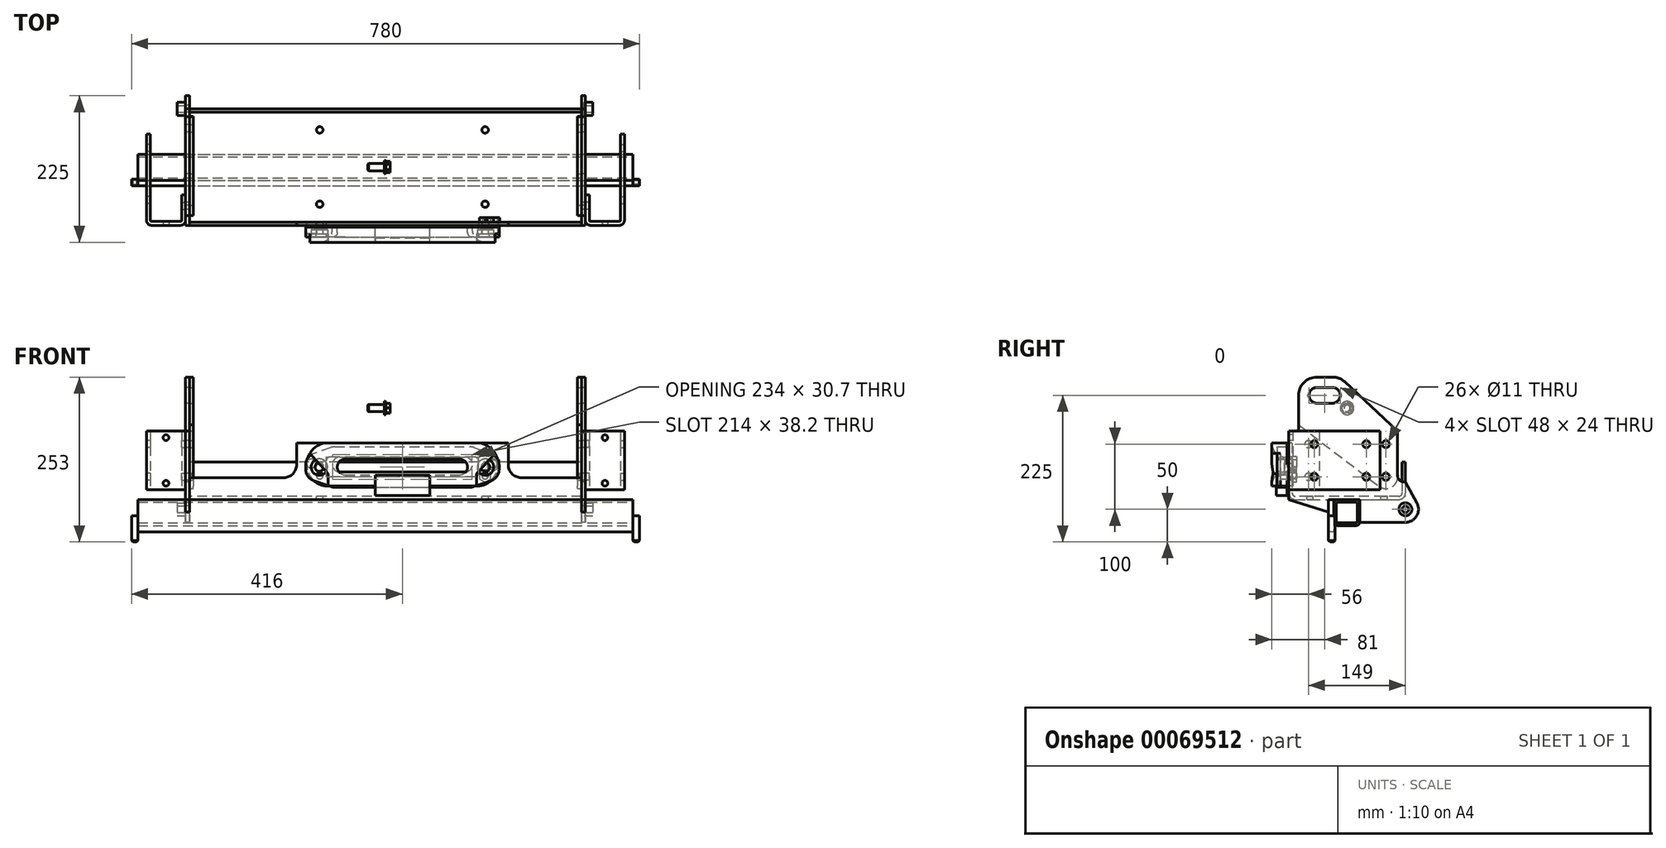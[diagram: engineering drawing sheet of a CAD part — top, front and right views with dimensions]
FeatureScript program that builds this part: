
annotation { "Feature Type Name" : "Feature", "Feature Type Description" : "" }
export const myFeature = defineFeature(function(context is Context, id is Id, definition is map)
    precondition{}
    {
        {
            var Q0;
            Q0=qCreatedBy(makeId("Right.planeOp"),FACE);
            var sketch = newSketch(context, id + "F0", { "sketchPlane" : qUnion([Q0])});
            skLineSegment(sketch, "E0", {"start": v(-84.5, 0) * mm, "end": v(84.5, 0) * mm});
            skLineSegment(sketch, "E1", {"start": v(-84.5, 0) * mm, "end": v(-84.5, 81.8) * mm});
            skLineSegment(sketch, "E2", {"start": v(84.5, 0) * mm, "end": v(84.5, 52.5) * mm});
            skLineSegment(sketch, "E3.0", {"start": v(-89.5, -5) * mm, "end": v(-89.5, 81.8) * mm});
            skLineSegment(sketch, "E3.1", {"start": v(-89.5, -5) * mm, "end": v(89.5, -5) * mm});
            skLineSegment(sketch, "E3.2", {"start": v(89.5, -5) * mm, "end": v(89.5, 52.5) * mm});
            skLineSegment(sketch, "E4", {"start": v(-89.5, 81.8) * mm, "end": v(-84.5, 81.8) * mm});
            skLineSegment(sketch, "E5", {"start": v(84.5, 52.5) * mm, "end": v(89.5, 52.5) * mm});
            skSolve(sketch);
        }
        {
            var Q0;
            Q0 = qSketchRegion(id + "F0", true);
            extrude(context, id + "F1", {"entities" : qUnion([Q0]), "endBound" : BoundingType.SYMMETRIC, "depth" : 896 * mm});
        }
        {
            var Q0;
            Q0=makeQuery(id+"F1.opExtrude","SWEPT_FACE",FACE,{"disambiguationData":[OSD([sQuery(id+"F0.wireOp",EDGE,"E3.0")])]});
            var sketch = newSketch(context, id + "F2", { "sketchPlane" : qUnion([Q0])});
            skLineSegment(sketch, "E6", {"start": v(-448, 28.5) * mm, "end": v(-162.5, 28.5) * mm});
            skLineSegment(sketch, "E7", {"start": v(-162.5, 28.5) * mm, "end": v(-162.5, 81.8) * mm});
            skLineSegment(sketch, "E8", {"start": v(-162.5, 81.8) * mm, "end": v(162.5, 81.8) * mm});
            skLineSegment(sketch, "E9", {"start": v(162.5, 81.8) * mm, "end": v(162.5, 28.5) * mm});
            skLineSegment(sketch, "E10", {"start": v(162.5, 28.5) * mm, "end": v(448, 28.5) * mm});
            skLineSegment(sketch, "E11.bottom", {"start": v(-117, 60.2) * mm, "end": v(117, 60.2) * mm});
            skLineSegment(sketch, "E11.top", {"start": v(-117, 29.5) * mm, "end": v(117, 29.5) * mm});
            skLineSegment(sketch, "E11.left", {"start": v(-117, 60.2) * mm, "end": v(-117, 29.5) * mm});
            skLineSegment(sketch, "E11.right", {"start": v(117, 60.2) * mm, "end": v(117, 29.5) * mm});
            skCircle(sketch, "E12", {"center": v(-140, 50.1) * mm, "radius": 6.9 * mm});
            skCircle(sketch, "E13", {"center": v(140, 50.1) * mm, "radius": 6.9 * mm});
            skCircle(sketch, "E14", {"center": v(-127, 31.5) * mm, "radius": 5.1 * mm});
            skCircle(sketch, "E15", {"center": v(127, 31.5) * mm, "radius": 5.1 * mm});
            skLineSegment(sketch, "E16", {"start": v(-140, 50.1) * mm, "end": v(140, 50.1) * mm, "construction": true});
            skLineSegment(sketch, "E17", {"start": v(0, 60.2) * mm, "end": v(0, 29.5) * mm, "construction": true});
            skCircle(sketch, "E18", {"center": v(-127.5, 44.85) * mm, "radius": 5.1 * mm});
            skCircle(sketch, "E19.MirrorC", {"center": v(127.5, 44.85) * mm, "radius": 5.1 * mm});
            skLineSegment(sketch, "E20", {"start": v(-117, 44.85) * mm, "end": v(117, 44.85) * mm, "construction": true});
            skLineSegment(sketch, "E21", {"start": v(-117, 44.85) * mm, "end": v(-162.5, 44.85) * mm, "construction": true});
            skCircle(sketch, "E22", {"center": v(-127.5, 44.85) * mm, "radius": 6 * mm, "construction": true});
            skCircle(sketch, "E23", {"center": v(-140, 50.1) * mm, "radius": 6 * mm, "construction": true});
            skLineSegment(sketch, "E24", {"start": v(-127.5, 44.85) * mm, "end": v(-127.5, 24.22) * mm, "construction": true});
            skSolve(sketch);
        }
        {
            var Q0;
            Q0 = qSketchRegion(id + "F2", true);
            var Q1;
            {var subQ0=sQuery(id+"F2.wireOp",EDGE,"E6");Q1=makeQuery(id+"F2.imprint","IMPRINT",FACE,{"disambiguationData":[TD([[makeQuery(id+"F2.imprint","IMPRINT",EDGE,{"derivedFrom":subQ0}),1.0]])]});}
            var Q2;
            {var subQ0=sQuery(id+"F2.wireOp",EDGE,"E9");Q2=makeQuery(id+"F2.imprint","IMPRINT",FACE,{"disambiguationData":[TD([[makeQuery(id+"F2.imprint","IMPRINT",EDGE,{"derivedFrom":subQ0}),1.0]])]});}
            extrude(context, id + "F3", {"entities" : qUnion([Q0, Q1, Q2]), "operationType" : NewBodyOperationType.REMOVE, "endBound" : BoundingType.UP_TO_NEXT, "oppositeDirection" : true, "depth" : 25 * mm});
        }
        {
            var Q0;
            Q0=makeQuery(id+"F1.opExtrude","SWEPT_FACE",FACE,{"disambiguationData":[OSD([sQuery(id+"F0.wireOp",EDGE,"E0")])]});
            var sketch = newSketch(context, id + "F4", { "sketchPlane" : qUnion([Q0])});
            skLineSegment(sketch, "E25.bottom", {"start": v(-127, 57) * mm, "end": v(127, 57) * mm, "construction": true});
            skLineSegment(sketch, "E25.top", {"start": v(-127, -57) * mm, "end": v(127, -57) * mm, "construction": true});
            skLineSegment(sketch, "E25.left", {"start": v(-127, 57) * mm, "end": v(-127, -57) * mm, "construction": true});
            skLineSegment(sketch, "E25.right", {"start": v(127, 57) * mm, "end": v(127, -57) * mm, "construction": true});
            skCircle(sketch, "E26", {"center": v(-127, 57) * mm, "radius": 5 * mm});
            skCircle(sketch, "E27", {"center": v(-127, -57) * mm, "radius": 5 * mm});
            skCircle(sketch, "E28", {"center": v(127, 57) * mm, "radius": 5 * mm});
            skCircle(sketch, "E29", {"center": v(127, -57) * mm, "radius": 5 * mm});
            skSolve(sketch);
        }
        {
            var Q0;
            Q0 = qSketchRegion(id + "F4", true);
            extrude(context, id + "F5", {"entities" : qUnion([Q0]), "operationType" : NewBodyOperationType.REMOVE, "endBound" : BoundingType.UP_TO_NEXT, "oppositeDirection" : true, "depth" : 25 * mm});
        }
        {
            var Q0;
            Q0=makeQuery(id+"F3.boolean.opBoolean","COPY",EDGE,{"derivedFrom":makeQuery(id+"F3.opExtrude","SWEPT_EDGE",EDGE,{"disambiguationData":[OSD([sQuery(id+"F2.wireOp",EDGE,"E6"),sQuery(id+"F2.wireOp",EDGE,"E7")])]})});
            var Q1;
            Q1=makeQuery(id+"F3.boolean.opBoolean","COPY",EDGE,{"derivedFrom":makeQuery(id+"F3.opExtrude","SWEPT_EDGE",EDGE,{"disambiguationData":[OSD([sQuery(id+"F0.wireOp",EDGE,"E3.0"),sQuery(id+"F0.wireOp",EDGE,"E4"),sQuery(id+"F2.wireOp",EDGE,"E7"),sQuery(id+"F2.wireOp",EDGE,"E8")])]})});
            var Q2;
            Q2=makeQuery(id+"F3.boolean.opBoolean","COPY",EDGE,{"derivedFrom":makeQuery(id+"F3.opExtrude","SWEPT_EDGE",EDGE,{"disambiguationData":[OSD([sQuery(id+"F0.wireOp",EDGE,"E3.0"),sQuery(id+"F0.wireOp",EDGE,"E4"),sQuery(id+"F2.wireOp",EDGE,"E8"),sQuery(id+"F2.wireOp",EDGE,"E9")])]})});
            var Q3;
            Q3=makeQuery(id+"F3.boolean.opBoolean","COPY",EDGE,{"derivedFrom":makeQuery(id+"F3.opExtrude","SWEPT_EDGE",EDGE,{"disambiguationData":[OSD([sQuery(id+"F2.wireOp",EDGE,"E9"),sQuery(id+"F2.wireOp",EDGE,"E10")])]})});
            fillet(context, id + "F6", {"entities" : qUnion([Q0, Q1, Q2, Q3]), "radius" : 20 * mm, "tangentPropagation" : true, "allowEdgeOverflow" : false});
        }
        {
            var Q0;
            Q0=makeQuery(id+"F3.boolean.opBoolean","COPY",EDGE,{"derivedFrom":makeQuery(id+"F3.opExtrude","SWEPT_EDGE",EDGE,{"disambiguationData":[OSD([sQuery(id+"F2.wireOp",EDGE,"E11.top"),sQuery(id+"F2.wireOp",EDGE,"E11.right")])]})});
            var Q1;
            Q1=makeQuery(id+"F3.boolean.opBoolean","COPY",EDGE,{"derivedFrom":makeQuery(id+"F3.opExtrude","SWEPT_EDGE",EDGE,{"disambiguationData":[OSD([sQuery(id+"F2.wireOp",EDGE,"E11.bottom"),sQuery(id+"F2.wireOp",EDGE,"E11.right")])]})});
            var Q2;
            Q2=makeQuery(id+"F3.boolean.opBoolean","COPY",EDGE,{"derivedFrom":makeQuery(id+"F3.opExtrude","SWEPT_EDGE",EDGE,{"disambiguationData":[OSD([sQuery(id+"F2.wireOp",EDGE,"E11.top"),sQuery(id+"F2.wireOp",EDGE,"E11.left")])]})});
            var Q3;
            Q3=makeQuery(id+"F3.boolean.opBoolean","COPY",EDGE,{"derivedFrom":makeQuery(id+"F3.opExtrude","SWEPT_EDGE",EDGE,{"disambiguationData":[OSD([sQuery(id+"F2.wireOp",EDGE,"E11.bottom"),sQuery(id+"F2.wireOp",EDGE,"E11.left")])]})});
            fillet(context, id + "F7", {"entities" : qUnion([Q0, Q1, Q2, Q3]), "radius" : 6 * mm, "allowEdgeOverflow" : false});
        }
        {
            var Q0;
            Q0=makeQuery(id+"F1.opExtrude","SWEPT_EDGE",EDGE,{"disambiguationData":[OSD([sQuery(id+"F0.wireOp",EDGE,"E0"),sQuery(id+"F0.wireOp",EDGE,"E2")])]});
            var Q1;
            Q1=makeQuery(id+"F1.opExtrude","SWEPT_EDGE",EDGE,{"disambiguationData":[OSD([sQuery(id+"F0.wireOp",EDGE,"E0"),sQuery(id+"F0.wireOp",EDGE,"E1")])]});
            fillet(context, id + "F8", {"entities" : qUnion([Q0, Q1]), "radius" : 5 * mm, "allowEdgeOverflow" : false});
        }
        {
            var Q0;
            Q0=makeQuery(id+"F1.opExtrude","SWEPT_EDGE",EDGE,{"disambiguationData":[OSD([sQuery(id+"F0.wireOp",EDGE,"E3.1"),sQuery(id+"F0.wireOp",EDGE,"E3.2")])]});
            var Q1;
            Q1=makeQuery(id+"F1.opExtrude","SWEPT_EDGE",EDGE,{"disambiguationData":[OSD([sQuery(id+"F0.wireOp",EDGE,"E3.0"),sQuery(id+"F0.wireOp",EDGE,"E3.1")])]});
            fillet(context, id + "F9", {"entities" : qUnion([Q0, Q1]), "radius" : 10 * mm, "allowEdgeOverflow" : false});
        }
        {
            var Q0;
            Q0=makeQuery(id+"F1.opExtrude","SWEPT_FACE",FACE,{"disambiguationData":[OSD([sQuery(id+"F0.wireOp",EDGE,"E3.0")])]});
            var sketch = newSketch(context, id + "F10", { "sketchPlane" : qUnion([Q0])});
            skCircle(sketch, "E30.0", {"center": v(-127, 31.5) * mm, "radius": 5.1 * mm});
            skCircle(sketch, "E31.0", {"center": v(127, 31.5) * mm, "radius": 5.1 * mm});
            skArc(sketch, "E32", {"start": v(-113.7, 82.1) * mm, "mid": v(-147, 48.8) * mm, "end": v(-113.7, 15.5) * mm});
            skArc(sketch, "E33", {"start": v(113.7, 15.5) * mm, "mid": v(147, 48.8) * mm, "end": v(113.7, 82.1) * mm});
            skLineSegment(sketch, "E34", {"start": v(-113.7, 82.1) * mm, "end": v(113.7, 82.1) * mm});
            skLineSegment(sketch, "E35", {"start": v(-113.7, 15.5) * mm, "end": v(-42, 15.5) * mm});
            skArc(sketch, "E36", {"start": v(-96, 60.3) * mm, "mid": v(-107.5, 48.8) * mm, "end": v(-96, 37.3) * mm});
            skArc(sketch, "E37", {"start": v(96, 37.3) * mm, "mid": v(107.5, 48.8) * mm, "end": v(96, 60.3) * mm});
            skLineSegment(sketch, "E38", {"start": v(-96, 60.3) * mm, "end": v(96, 60.3) * mm});
            skLineSegment(sketch, "E39", {"start": v(-96, 37.3) * mm, "end": v(96, 37.3) * mm});
            skLineSegment(sketch, "E40.top", {"start": v(-42, 1.1) * mm, "end": v(42, 1.1) * mm});
            skLineSegment(sketch, "E40.left", {"start": v(-42, 15.5) * mm, "end": v(-42, 1.1) * mm});
            skLineSegment(sketch, "E40.right", {"start": v(42, 15.5) * mm, "end": v(42, 1.1) * mm});
            skLineSegment(sketch, "E41.trimOffspring", {"start": v(42, 15.5) * mm, "end": v(113.7, 15.5) * mm});
            skSolve(sketch);
        }
        {
            var Q0;
            Q0 = qSketchRegion(id + "F10", true);
            extrude(context, id + "F11", {"entities" : qUnion([Q0]), "depth" : 23 * mm});
        }
        {
            var Q0;
            Q0=makeQuery(id+"F11.opExtrude","SWEPT_BODY",BODY,{"disambiguationData":[OSD([sQuery(id+"F10.wireOp",EDGE,"E30.0"),sQuery(id+"F10.wireOp",EDGE,"E31.0"),sQuery(id+"F10.wireOp",EDGE,"E32"),sQuery(id+"F10.wireOp",EDGE,"E33"),sQuery(id+"F10.wireOp",EDGE,"E34"),sQuery(id+"F10.wireOp",EDGE,"E35"),sQuery(id+"F10.wireOp",EDGE,"E36"),sQuery(id+"F10.wireOp",EDGE,"E37"),sQuery(id+"F10.wireOp",EDGE,"E38"),sQuery(id+"F10.wireOp",EDGE,"E39"),sQuery(id+"F10.wireOp",EDGE,"E40.top"),sQuery(id+"F10.wireOp",EDGE,"E40.left"),sQuery(id+"F10.wireOp",EDGE,"E40.right"),sQuery(id+"F10.wireOp",EDGE,"E41.trimOffspring")])]});
            transform(context, id + "F12", {"entities" : qUnion([Q0]), "transformType" : TransformType.TRANSLATION_3D, "dx" : 0 * mm, "dy" : -3 * mm, "dz" : 0 * mm, "makeCopy" : false});
        }
        {
            var Q0;
            Q0=makeQuery(id+"F11.opExtrude","CAP_EDGE",EDGE,{"disambiguationData":[OSD([sQuery(id+"F10.wireOp",EDGE,"E37")])],"isStart":false});
            fillet(context, id + "F13", {"entities" : qUnion([Q0]), "radius" : 20 * mm, "tangentPropagation" : true, "allowEdgeOverflow" : false});
        }
        {
            var Q0;
            Q0=makeQuery(id+"F11.opExtrude","CAP_FACE",FACE,{"disambiguationData":[OSD([sQuery(id+"F10.wireOp",EDGE,"E30.0"),sQuery(id+"F10.wireOp",EDGE,"E31.0"),sQuery(id+"F10.wireOp",EDGE,"E32"),sQuery(id+"F10.wireOp",EDGE,"E33"),sQuery(id+"F10.wireOp",EDGE,"E34"),sQuery(id+"F10.wireOp",EDGE,"E35"),sQuery(id+"F10.wireOp",EDGE,"E36"),sQuery(id+"F10.wireOp",EDGE,"E37"),sQuery(id+"F10.wireOp",EDGE,"E38"),sQuery(id+"F10.wireOp",EDGE,"E39"),sQuery(id+"F10.wireOp",EDGE,"E40.top"),sQuery(id+"F10.wireOp",EDGE,"E40.left"),sQuery(id+"F10.wireOp",EDGE,"E40.right"),sQuery(id+"F10.wireOp",EDGE,"E41.trimOffspring")])],"isStart":false});
            var sketch = newSketch(context, id + "F14", { "sketchPlane" : qUnion([Q0])});
            skLineSegment(sketch, "E42.bottom", {"start": v(-42, 1.1) * mm, "end": v(42, 1.1) * mm});
            skLineSegment(sketch, "E42.top", {"start": v(-42, 40.98) * mm, "end": v(42, 40.98) * mm});
            skLineSegment(sketch, "E42.left", {"start": v(-42, 1.1) * mm, "end": v(-42, 40.98) * mm});
            skLineSegment(sketch, "E42.right", {"start": v(42, 1.1) * mm, "end": v(42, 40.98) * mm});
            skSolve(sketch);
        }
        {
            var Q0;
            Q0 = qSketchRegion(id + "F14", true);
            extrude(context, id + "F15", {"entities" : qUnion([Q0]), "operationType" : NewBodyOperationType.REMOVE, "oppositeDirection" : true, "depth" : 6.5 * mm});
        }
        {
            var Q0;
            Q0=makeQuery(id+"F11.opExtrude","CAP_FACE",FACE,{"disambiguationData":[OSD([sQuery(id+"F10.wireOp",EDGE,"E30.0"),sQuery(id+"F10.wireOp",EDGE,"E31.0"),sQuery(id+"F10.wireOp",EDGE,"E32"),sQuery(id+"F10.wireOp",EDGE,"E33"),sQuery(id+"F10.wireOp",EDGE,"E34"),sQuery(id+"F10.wireOp",EDGE,"E35"),sQuery(id+"F10.wireOp",EDGE,"E36"),sQuery(id+"F10.wireOp",EDGE,"E37"),sQuery(id+"F10.wireOp",EDGE,"E38"),sQuery(id+"F10.wireOp",EDGE,"E39"),sQuery(id+"F10.wireOp",EDGE,"E40.top"),sQuery(id+"F10.wireOp",EDGE,"E40.left"),sQuery(id+"F10.wireOp",EDGE,"E40.right"),sQuery(id+"F10.wireOp",EDGE,"E41.trimOffspring")])],"isStart":false});
            var sketch = newSketch(context, id + "F16", { "sketchPlane" : qUnion([Q0])});
            skArc(sketch, "E43.0", {"start": v(-142.15, 66.1) * mm, "mid": v(-142.8, 32.6) * mm, "end": v(-114, 15.5) * mm});
            skLineSegment(sketch, "E44", {"start": v(-142.15, 66.1) * mm, "end": v(-114, 34.5) * mm});
            skLineSegment(sketch, "E45", {"start": v(-114, 34.5) * mm, "end": v(-114, 15.5) * mm});
            skLineSegment(sketch, "E46", {"start": v(0, -35.84) * mm, "end": v(0, 92.87) * mm, "construction": true});
            skLineSegment(sketch, "E47.MirrorCS", {"start": v(142.15, 66.1) * mm, "end": v(114, 34.5) * mm});
            skArc(sketch, "E48.MirrorCS", {"start": v(142.15, 66.1) * mm, "mid": v(142.8, 32.6) * mm, "end": v(114, 15.5) * mm});
            skLineSegment(sketch, "E49.MirrorCS", {"start": v(114, 34.5) * mm, "end": v(114, 15.5) * mm});
            skSolve(sketch);
        }
        {
            var Q0;
            Q0 = qSketchRegion(id + "F16", true);
            extrude(context, id + "F17", {"entities" : qUnion([Q0]), "operationType" : NewBodyOperationType.REMOVE, "oppositeDirection" : true, "depth" : 13 * mm});
        }
        {
            var Q0;
            Q0=makeQuery(id+"F1.opExtrude","SWEPT_FACE",FACE,{"disambiguationData":[OSD([sQuery(id+"F0.wireOp",EDGE,"E3.1")])]});
            var sketch = newSketch(context, id + "F18", { "sketchPlane" : qUnion([Q0])});
            skLineSegment(sketch, "E50.bottom", {"start": v(448, 89.58) * mm, "end": v(275, 89.58) * mm});
            skLineSegment(sketch, "E50.top", {"start": v(448, -89.63) * mm, "end": v(275, -89.63) * mm});
            skLineSegment(sketch, "E50.left", {"start": v(448, 89.58) * mm, "end": v(448, -89.63) * mm});
            skLineSegment(sketch, "E50.right", {"start": v(275, 89.58) * mm, "end": v(275, -89.63) * mm});
            skLineSegment(sketch, "E51.bottom", {"start": v(-448, 89.51) * mm, "end": v(-327, 89.51) * mm});
            skLineSegment(sketch, "E51.top", {"start": v(-448, -89.5) * mm, "end": v(-327, -89.5) * mm});
            skLineSegment(sketch, "E51.left", {"start": v(-448, 89.51) * mm, "end": v(-448, -89.5) * mm});
            skLineSegment(sketch, "E51.right", {"start": v(-327, 89.51) * mm, "end": v(-327, -89.5) * mm});
            skSolve(sketch);
        }
        {
            var Q0;
            Q0 = qSketchRegion(id + "F18", true);
            extrude(context, id + "F19", {"entities" : qUnion([Q0]), "operationType" : NewBodyOperationType.REMOVE, "endBound" : BoundingType.THROUGH_ALL, "oppositeDirection" : true, "depth" : 25 * mm});
        }
        {
            var Q0;
            Q0=makeQuery(id+"F19.boolean.opBoolean","COPY",FACE,{"derivedFrom":makeQuery(id+"F19.opExtrude","SWEPT_FACE",FACE,{"disambiguationData":[OSD([sQuery(id+"F18.wireOp",EDGE,"E50.right")])]})});
            var sketch = newSketch(context, id + "F20", { "sketchPlane" : qUnion([Q0])});
            skCircle(sketch, "E52", {"center": v(89.5, -20) * mm, "radius": 5.5 * mm});
            skCircle(sketch, "E53", {"center": v(59.5, 30) * mm, "radius": 5.5 * mm});
            skCircle(sketch, "E54", {"center": v(59.5, 80) * mm, "radius": 5.5 * mm});
            skLineSegment(sketch, "E55", {"start": v(-89.5, 100) * mm, "end": v(-89.5, -5) * mm});
            skLineSegment(sketch, "E56", {"start": v(-28.7, -24.52) * mm, "end": v(-28.7, -5) * mm});
            skLineSegment(sketch, "E57", {"start": v(-28.7, -5) * mm, "end": v(19.5, -5) * mm});
            skLineSegment(sketch, "E58", {"start": v(19.5, -5) * mm, "end": v(19.5, -40) * mm});
            skLineSegment(sketch, "E59", {"start": v(19.5, -40) * mm, "end": v(89.5, -40) * mm});
            skArc(sketch, "E60", {"start": v(89.5, -40) * mm, "mid": v(106.68, -30.24) * mm, "end": v(107.09, -10.48) * mm});
            skLineSegment(sketch, "E61", {"start": v(89.5, 22) * mm, "end": v(107.09, -10.48) * mm});
            skLineSegment(sketch, "E62", {"start": v(89.5, 22) * mm, "end": v(87.5, 22) * mm});
            skLineSegment(sketch, "E63", {"start": v(77.5, 32) * mm, "end": v(77.5, 100) * mm});
            skLineSegment(sketch, "E64", {"start": v(-22.5, 183) * mm, "end": v(-46.5, 183) * mm});
            skLineSegment(sketch, "E65", {"start": v(-79.5, 100) * mm, "end": v(-89.5, 100) * mm});
            skCircle(sketch, "E66", {"center": v(-46.5, 155) * mm, "radius": 12 * mm});
            skCircle(sketch, "E67", {"center": v(-22.5, 155) * mm, "radius": 12 * mm});
            skLineSegment(sketch, "E68", {"start": v(-46.5, 167) * mm, "end": v(-22.5, 167) * mm});
            skLineSegment(sketch, "E69", {"start": v(-46.5, 143) * mm, "end": v(-22.5, 143) * mm});
            skPoint(sketch, "E70.visualSharp", {"position": v(-45.45, 100) * mm});
            skArc(sketch, "E70.filletArc", {"start": v(-79.5, 100) * mm, "mid": v(-75.96, 101.46) * mm, "end": v(-74.5, 105) * mm});
            skPoint(sketch, "E71.visualSharp", {"position": v(77.5, 22) * mm});
            skArc(sketch, "E71.filletArc", {"start": v(77.5, 32) * mm, "mid": v(80.43, 24.93) * mm, "end": v(87.5, 22) * mm});
            skArc(sketch, "E72", {"start": v(-3.4, 175.47) * mm, "mid": v(-12.24, 181.05) * mm, "end": v(-22.5, 183) * mm});
            skArc(sketch, "E73", {"start": v(-46.5, 183) * mm, "mid": v(-66.3, 174.8) * mm, "end": v(-74.5, 155) * mm});
            skLineSegment(sketch, "E74", {"start": v(-89.5, -5) * mm, "end": v(19.5, -40) * mm, "construction": true});
            skLineSegment(sketch, "E75", {"start": v(-89.5, -5) * mm, "end": v(-28.7, -24.52) * mm});
            skLineSegment(sketch, "E76", {"start": v(-79.5, 100) * mm, "end": v(77.5, 100) * mm, "construction": true});
            skLineSegment(sketch, "E77", {"start": v(77.5, 100) * mm, "end": v(-3.4, 175.47) * mm});
            skLineSegment(sketch, "E78", {"start": v(-74.5, 105) * mm, "end": v(-74.5, 155) * mm});
            skSolve(sketch);
        }
        {
            var Q0;
            Q0 = qSketchRegion(id + "F20", true);
            extrude(context, id + "F21", {"entities" : qUnion([Q0]), "depth" : 6 * mm});
        }
        {
            var Q0;
            Q0=makeQuery(id+"F21.opExtrude","SWEPT_BODY",BODY,{"disambiguationData":[OSD([sQuery(id+"F20.wireOp",EDGE,"E52"),sQuery(id+"F20.wireOp",EDGE,"E53"),sQuery(id+"F20.wireOp",EDGE,"E54"),sQuery(id+"F20.wireOp",EDGE,"E55"),sQuery(id+"F20.wireOp",EDGE,"XvVVhRg5-2krd-yFCo-rq4G-s1C9oEQ6HOLZ"),sQuery(id+"F20.wireOp",EDGE,"E56"),sQuery(id+"F20.wireOp",EDGE,"E57"),sQuery(id+"F20.wireOp",EDGE,"E58"),sQuery(id+"F20.wireOp",EDGE,"E59"),sQuery(id+"F20.wireOp",EDGE,"E60"),sQuery(id+"F20.wireOp",EDGE,"E61"),sQuery(id+"F20.wireOp",EDGE,"E62"),sQuery(id+"F20.wireOp",EDGE,"E63"),sQuery(id+"F20.wireOp",EDGE,"E64"),sQuery(id+"F20.wireOp",EDGE,"lX6jeAK8-40P4-eBXy-fJTd-rd2ZCsxYktxP"),sQuery(id+"F20.wireOp",EDGE,"E65"),sQuery(id+"F20.wireOp",EDGE,"E66"),sQuery(id+"F20.wireOp",EDGE,"E67"),sQuery(id+"F20.wireOp",EDGE,"E68"),sQuery(id+"F20.wireOp",EDGE,"E69")])]});
            var Q1;
            {var subQ0=sQuery(id+"F0.wireOp",EDGE,"E0");Q1=makeQuery(id+"F8.opFillet","BLEND_EDGE",EDGE,{"blendedFrom":[makeQuery(id+"F1.opExtrude","SWEPT_EDGE",EDGE,{"disambiguationData":[OSD([subQ0,sQuery(id+"F0.wireOp",EDGE,"E2")])]}),makeQuery(id+"F1.opExtrude","SWEPT_FACE",FACE,{"disambiguationData":[OSD([subQ0])]})],"blendedInto":[makeQuery(id+"F1.opExtrude","SWEPT_FACE",FACE,{"disambiguationData":[OSD([subQ0])]})]});}
            var Q2;
            {var subQ0=sQuery(id+"F0.wireOp",EDGE,"E0");Q2=makeQuery(id+"F8.opFillet","BLEND_EDGE",EDGE,{"blendedFrom":[makeQuery(id+"F1.opExtrude","SWEPT_EDGE",EDGE,{"disambiguationData":[OSD([subQ0,sQuery(id+"F0.wireOp",EDGE,"E2")])]}),makeQuery(id+"F1.opExtrude","SWEPT_FACE",FACE,{"disambiguationData":[OSD([subQ0])]})],"blendedInto":[makeQuery(id+"F1.opExtrude","SWEPT_FACE",FACE,{"disambiguationData":[OSD([subQ0])]})]});}
            transform(context, id + "F22", {"entities" : qUnion([Q0]), "transformType" : TransformType.TRANSLATION_DISTANCE, "transformDirection" : qUnion([Q2]), "distance" : 608 * mm, "makeCopy" : true});
        }
        {
            var Q0;
            Q0=makeQuery(id+"F21.opExtrude","CAP_FACE",FACE,{"disambiguationData":[OSD([sQuery(id+"F20.wireOp",EDGE,"E52"),sQuery(id+"F20.wireOp",EDGE,"E53"),sQuery(id+"F20.wireOp",EDGE,"E54"),sQuery(id+"F20.wireOp",EDGE,"E55"),sQuery(id+"F20.wireOp",EDGE,"E56"),sQuery(id+"F20.wireOp",EDGE,"E57"),sQuery(id+"F20.wireOp",EDGE,"E58"),sQuery(id+"F20.wireOp",EDGE,"E59"),sQuery(id+"F20.wireOp",EDGE,"E60"),sQuery(id+"F20.wireOp",EDGE,"E61"),sQuery(id+"F20.wireOp",EDGE,"E62"),sQuery(id+"F20.wireOp",EDGE,"E63"),sQuery(id+"F20.wireOp",EDGE,"E64"),sQuery(id+"F20.wireOp",EDGE,"E65"),sQuery(id+"F20.wireOp",EDGE,"E66"),sQuery(id+"F20.wireOp",EDGE,"E67"),sQuery(id+"F20.wireOp",EDGE,"E68"),sQuery(id+"F20.wireOp",EDGE,"E69"),sQuery(id+"F20.wireOp",EDGE,"E70.filletArc"),sQuery(id+"F20.wireOp",EDGE,"E71.filletArc"),sQuery(id+"F20.wireOp",EDGE,"E72"),sQuery(id+"F20.wireOp",EDGE,"E73"),sQuery(id+"F20.wireOp",EDGE,"E75"),sQuery(id+"F20.wireOp",EDGE,"E77"),sQuery(id+"F20.wireOp",EDGE,"E78")])],"isStart":true});
            var sketch = newSketch(context, id + "F23", { "sketchPlane" : qUnion([Q0])});
            skCircle(sketch, "E79.0", {"center": v(-59.5, 30) * mm, "radius": 5.5 * mm});
            skCircle(sketch, "E80.0", {"center": v(-59.5, 80) * mm, "radius": 5.5 * mm});
            skLineSegment(sketch, "E81.0", {"start": v(-77.5, 100) * mm, "end": v(3.4, 175.47) * mm});
            skArc(sketch, "E82.0", {"start": v(3.4, 175.47) * mm, "mid": v(12.24, 181.05) * mm, "end": v(22.5, 183) * mm});
            skLineSegment(sketch, "E83.0", {"start": v(22.5, 183) * mm, "end": v(46.5, 183) * mm});
            skArc(sketch, "E84.0", {"start": v(46.5, 183) * mm, "mid": v(66.3, 174.8) * mm, "end": v(74.5, 155) * mm});
            skArc(sketch, "E85.0", {"start": v(46.5, 167) * mm, "mid": v(58.5, 155) * mm, "end": v(46.5, 143) * mm});
            skLineSegment(sketch, "E86.0", {"start": v(46.5, 167) * mm, "end": v(22.5, 167) * mm});
            skArc(sketch, "E87.0", {"start": v(22.5, 143) * mm, "mid": v(10.5, 155) * mm, "end": v(22.5, 167) * mm});
            skLineSegment(sketch, "E88.0", {"start": v(46.5, 143) * mm, "end": v(22.5, 143) * mm});
            skCircle(sketch, "E89", {"center": v(-59.5, 30) * mm, "radius": 18.21 * mm});
            skLineSegment(sketch, "E90", {"start": v(-77.5, 100) * mm, "end": v(-77.5, 27.23) * mm});
            skLineSegment(sketch, "E91", {"start": v(74.5, 155) * mm, "end": v(74.5, 110) * mm});
            skLineSegment(sketch, "E92", {"start": v(74.5, 110) * mm, "end": v(-48.4, 15.56) * mm});
            skSolve(sketch);
        }
        {
            var Q0;
            Q0 = qSketchRegion(id + "F23", true);
            extrude(context, id + "F24", {"entities" : qUnion([Q0]), "depth" : 6 * mm});
        }
        {
            var Q0;
            Q0=makeQuery(id+"F24.opExtrude","SWEPT_BODY",BODY,{"disambiguationData":[OSD([sQuery(id+"F23.wireOp",EDGE,"E79.0"),sQuery(id+"F23.wireOp",EDGE,"E80.0"),sQuery(id+"F23.wireOp",EDGE,"E81.0"),sQuery(id+"F23.wireOp",EDGE,"E82.0"),sQuery(id+"F23.wireOp",EDGE,"E83.0"),sQuery(id+"F23.wireOp",EDGE,"E84.0"),sQuery(id+"F23.wireOp",EDGE,"E85.0"),sQuery(id+"F23.wireOp",EDGE,"E86.0"),sQuery(id+"F23.wireOp",EDGE,"E87.0"),sQuery(id+"F23.wireOp",EDGE,"E88.0"),sQuery(id+"F23.wireOp",EDGE,"E89"),sQuery(id+"F23.wireOp",EDGE,"E90"),sQuery(id+"F23.wireOp",EDGE,"E91"),sQuery(id+"F23.wireOp",EDGE,"E92")])]});
            var Q1;
            Q1=makeQuery(id+"F1.opExtrude","SWEPT_EDGE",EDGE,{"disambiguationData":[OSD([sQuery(id+"F0.wireOp",EDGE,"E2"),sQuery(id+"F0.wireOp",EDGE,"E5")])]});
            transform(context, id + "F25", {"entities" : qUnion([Q0]), "transformType" : TransformType.TRANSLATION_DISTANCE, "transformDirection" : qUnion([Q1]), "distance" : 596 * mm, "makeCopy" : true});
        }
        {
            var Q0;
            Q0=makeQuery(id+"F21.opExtrude","CAP_FACE",FACE,{"disambiguationData":[OSD([sQuery(id+"F20.wireOp",EDGE,"E52"),sQuery(id+"F20.wireOp",EDGE,"E53"),sQuery(id+"F20.wireOp",EDGE,"E54"),sQuery(id+"F20.wireOp",EDGE,"E55"),sQuery(id+"F20.wireOp",EDGE,"XvVVhRg5-2krd-yFCo-rq4G-s1C9oEQ6HOLZ"),sQuery(id+"F20.wireOp",EDGE,"E56"),sQuery(id+"F20.wireOp",EDGE,"E57"),sQuery(id+"F20.wireOp",EDGE,"E58"),sQuery(id+"F20.wireOp",EDGE,"E59"),sQuery(id+"F20.wireOp",EDGE,"E60"),sQuery(id+"F20.wireOp",EDGE,"E61"),sQuery(id+"F20.wireOp",EDGE,"E62"),sQuery(id+"F20.wireOp",EDGE,"E63"),sQuery(id+"F20.wireOp",EDGE,"E64"),sQuery(id+"F20.wireOp",EDGE,"lX6jeAK8-40P4-eBXy-fJTd-rd2ZCsxYktxP"),sQuery(id+"F20.wireOp",EDGE,"E65"),sQuery(id+"F20.wireOp",EDGE,"E66"),sQuery(id+"F20.wireOp",EDGE,"E67"),sQuery(id+"F20.wireOp",EDGE,"E68"),sQuery(id+"F20.wireOp",EDGE,"E69")])],"isStart":false});
            var sketch = newSketch(context, id + "F26", { "sketchPlane" : qUnion([Q0])});
            skLineSegment(sketch, "E93.bottom", {"start": v(-14.5, -5) * mm, "end": v(13.5, -5) * mm});
            skLineSegment(sketch, "E93.top", {"start": v(-14.5, -45) * mm, "end": v(13.5, -45) * mm});
            skLineSegment(sketch, "E93.left", {"start": v(-20.5, -11) * mm, "end": v(-20.5, -39) * mm});
            skLineSegment(sketch, "E93.right", {"start": v(19.5, -11) * mm, "end": v(19.5, -39) * mm});
            skPoint(sketch, "E94.visualSharp", {"position": v(-20.5, -5) * mm});
            skArc(sketch, "E94.filletArc", {"start": v(-14.5, -5) * mm, "mid": v(-18.74, -6.76) * mm, "end": v(-20.5, -11) * mm});
            skPoint(sketch, "E95.visualSharp", {"position": v(19.5, -5) * mm});
            skArc(sketch, "E95.filletArc", {"start": v(19.5, -11) * mm, "mid": v(17.74, -6.76) * mm, "end": v(13.5, -5) * mm});
            skPoint(sketch, "E96.visualSharp", {"position": v(19.5, -45) * mm});
            skArc(sketch, "E96.filletArc", {"start": v(13.5, -45) * mm, "mid": v(17.74, -43.24) * mm, "end": v(19.5, -39) * mm});
            skPoint(sketch, "E97.visualSharp", {"position": v(-20.5, -45) * mm});
            skArc(sketch, "E97.filletArc", {"start": v(-20.5, -39) * mm, "mid": v(-18.74, -43.24) * mm, "end": v(-14.5, -45) * mm});
            skLineSegment(sketch, "E98.0", {"start": v(-14.5, -9) * mm, "end": v(13.5, -9) * mm});
            skArc(sketch, "E98.1", {"start": v(15.5, -11) * mm, "mid": v(14.91, -9.59) * mm, "end": v(13.5, -9) * mm});
            skArc(sketch, "E98.2", {"start": v(-14.5, -9) * mm, "mid": v(-15.91, -9.59) * mm, "end": v(-16.5, -11) * mm});
            skLineSegment(sketch, "E98.3", {"start": v(15.5, -11) * mm, "end": v(15.5, -39) * mm});
            skLineSegment(sketch, "E98.4", {"start": v(-16.5, -11) * mm, "end": v(-16.5, -39) * mm});
            skArc(sketch, "E98.5", {"start": v(-16.5, -39) * mm, "mid": v(-15.91, -40.41) * mm, "end": v(-14.5, -41) * mm});
            skLineSegment(sketch, "E98.6", {"start": v(-14.5, -41) * mm, "end": v(13.5, -41) * mm});
            skArc(sketch, "E98.7", {"start": v(13.5, -41) * mm, "mid": v(14.91, -40.41) * mm, "end": v(15.5, -39) * mm});
            skSolve(sketch);
        }
        {
            var Q0;
            Q0 = qSketchRegion(id + "F26", true);
            extrude(context, id + "F27", {"entities" : qUnion([Q0]), "oppositeDirection" : true, "depth" : 687 * mm, "hasSecondDirection" : true, "secondDirectionOppositeDirection" : false, "secondDirectionDepth" : 73 * mm});
        }
        {
            var Q0;
            Q0=makeQuery(id+"F21.opExtrude","CAP_FACE",FACE,{"disambiguationData":[OSD([sQuery(id+"F20.wireOp",EDGE,"E52"),sQuery(id+"F20.wireOp",EDGE,"E53"),sQuery(id+"F20.wireOp",EDGE,"E54"),sQuery(id+"F20.wireOp",EDGE,"E55"),sQuery(id+"F20.wireOp",EDGE,"XvVVhRg5-2krd-yFCo-rq4G-s1C9oEQ6HOLZ"),sQuery(id+"F20.wireOp",EDGE,"E56"),sQuery(id+"F20.wireOp",EDGE,"E57"),sQuery(id+"F20.wireOp",EDGE,"E58"),sQuery(id+"F20.wireOp",EDGE,"E59"),sQuery(id+"F20.wireOp",EDGE,"E60"),sQuery(id+"F20.wireOp",EDGE,"E61"),sQuery(id+"F20.wireOp",EDGE,"E62"),sQuery(id+"F20.wireOp",EDGE,"E63"),sQuery(id+"F20.wireOp",EDGE,"E64"),sQuery(id+"F20.wireOp",EDGE,"lX6jeAK8-40P4-eBXy-fJTd-rd2ZCsxYktxP"),sQuery(id+"F20.wireOp",EDGE,"E65"),sQuery(id+"F20.wireOp",EDGE,"E66"),sQuery(id+"F20.wireOp",EDGE,"E67"),sQuery(id+"F20.wireOp",EDGE,"E68"),sQuery(id+"F20.wireOp",EDGE,"E69")])],"isStart":true});
            var sketch = newSketch(context, id + "F28", { "sketchPlane" : qUnion([Q0])});
            skLineSegment(sketch, "E99.bottom", {"start": v(20.5, -5) * mm, "end": v(28.5, -5) * mm});
            skLineSegment(sketch, "E99.top", {"start": v(20.5, -55) * mm, "end": v(28.5, -55) * mm});
            skLineSegment(sketch, "E99.left", {"start": v(20.5, -5) * mm, "end": v(20.5, -55) * mm});
            skLineSegment(sketch, "E99.right", {"start": v(28.5, -5) * mm, "end": v(28.5, -55) * mm});
            skSolve(sketch);
        }
        {
            var Q0;
            Q0 = qSketchRegion(id + "F28", true);
            var Q1;
            Q1=makeQuery(id+"F22.opPattern","COPY",BODY,{"derivedFrom":makeQuery(id+"F21.opExtrude","SWEPT_BODY",BODY,{"disambiguationData":[OSD([sQuery(id+"F20.wireOp",EDGE,"E52"),sQuery(id+"F20.wireOp",EDGE,"E53"),sQuery(id+"F20.wireOp",EDGE,"E54"),sQuery(id+"F20.wireOp",EDGE,"E55"),sQuery(id+"F20.wireOp",EDGE,"XvVVhRg5-2krd-yFCo-rq4G-s1C9oEQ6HOLZ"),sQuery(id+"F20.wireOp",EDGE,"E56"),sQuery(id+"F20.wireOp",EDGE,"E57"),sQuery(id+"F20.wireOp",EDGE,"E58"),sQuery(id+"F20.wireOp",EDGE,"E59"),sQuery(id+"F20.wireOp",EDGE,"E60"),sQuery(id+"F20.wireOp",EDGE,"E61"),sQuery(id+"F20.wireOp",EDGE,"E62"),sQuery(id+"F20.wireOp",EDGE,"E63"),sQuery(id+"F20.wireOp",EDGE,"E64"),sQuery(id+"F20.wireOp",EDGE,"lX6jeAK8-40P4-eBXy-fJTd-rd2ZCsxYktxP"),sQuery(id+"F20.wireOp",EDGE,"E65"),sQuery(id+"F20.wireOp",EDGE,"E66"),sQuery(id+"F20.wireOp",EDGE,"E67"),sQuery(id+"F20.wireOp",EDGE,"E68"),sQuery(id+"F20.wireOp",EDGE,"E69")])]}),"instanceName":"1"});
            extrude(context, id + "F29", {"entities" : qUnion([Q0]), "endBoundEntityBody" : qUnion([Q1]), "depth" : 681 * mm, "hasSecondDirection" : true, "secondDirectionOppositeDirection" : true, "secondDirectionDepth" : 79 * mm});
        }
        {
            var Q0;
            Q0=qCreatedBy(makeId("Top.planeOp"),FACE);
            var sketch = newSketch(context, id + "F30", { "sketchPlane" : qUnion([Q0])});
            skLineSegment(sketch, "E100", {"start": v(281, -42.5) * mm, "end": v(281, -81.5) * mm});
            skLineSegment(sketch, "E101", {"start": v(289, -89.5) * mm, "end": v(333, -89.5) * mm});
            skLineSegment(sketch, "E102", {"start": v(341, -81.5) * mm, "end": v(341, 50.5) * mm});
            skPoint(sketch, "E103.visualSharp", {"position": v(281, -89.5) * mm});
            skArc(sketch, "E103.filletArc", {"start": v(281, -81.5) * mm, "mid": v(283.34, -87.16) * mm, "end": v(289, -89.5) * mm});
            skPoint(sketch, "E104.visualSharp", {"position": v(341, -89.5) * mm});
            skArc(sketch, "E104.filletArc", {"start": v(333, -89.5) * mm, "mid": v(338.66, -87.16) * mm, "end": v(341, -81.5) * mm});
            skLineSegment(sketch, "E105.0", {"start": v(335, -81.5) * mm, "end": v(335, 50.5) * mm});
            skLineSegment(sketch, "E105.1", {"start": v(287, -42.5) * mm, "end": v(287, -81.5) * mm});
            skArc(sketch, "E105.2", {"start": v(287, -81.5) * mm, "mid": v(287.59, -82.91) * mm, "end": v(289, -83.5) * mm});
            skLineSegment(sketch, "E105.3", {"start": v(289, -83.5) * mm, "end": v(333, -83.5) * mm});
            skArc(sketch, "E105.4", {"start": v(333, -83.5) * mm, "mid": v(334.41, -82.91) * mm, "end": v(335, -81.5) * mm});
            skLineSegment(sketch, "E106", {"start": v(281, -42.5) * mm, "end": v(287, -42.5) * mm});
            skLineSegment(sketch, "E107", {"start": v(335, 50.5) * mm, "end": v(341, 50.5) * mm});
            skSolve(sketch);
        }
        {
            var Q0;
            Q0 = qSketchRegion(id + "F30", true);
            extrude(context, id + "F31", {"entities" : qUnion([Q0]), "depth" : 90 * mm});
        }
        {
            var Q0;
            Q0=makeQuery(id+"F31.opExtrude","SWEPT_BODY",BODY,{"disambiguationData":[OSD([sQuery(id+"F30.wireOp",EDGE,"E100"),sQuery(id+"F30.wireOp",EDGE,"E101"),sQuery(id+"F30.wireOp",EDGE,"E102"),sQuery(id+"F30.wireOp",EDGE,"E103.filletArc"),sQuery(id+"F30.wireOp",EDGE,"E104.filletArc"),sQuery(id+"F30.wireOp",EDGE,"E105.0"),sQuery(id+"F30.wireOp",EDGE,"E105.1"),sQuery(id+"F30.wireOp",EDGE,"E105.2"),sQuery(id+"F30.wireOp",EDGE,"E105.3"),sQuery(id+"F30.wireOp",EDGE,"E105.4"),sQuery(id+"F30.wireOp",EDGE,"E106"),sQuery(id+"F30.wireOp",EDGE,"E107")])]});
            transform(context, id + "F32", {"entities" : qUnion([Q0]), "transformType" : TransformType.TRANSLATION_3D, "dx" : 0 * mm, "dy" : 0 * mm, "dz" : 10 * mm, "makeCopy" : false});
        }
        {
            var Q0;
            Q0=makeQuery(id+"F31.opExtrude","SWEPT_FACE",FACE,{"disambiguationData":[OSD([sQuery(id+"F30.wireOp",EDGE,"E102")])]});
            var sketch = newSketch(context, id + "F33", { "sketchPlane" : qUnion([Q0])});
            skLineSegment(sketch, "E108.bottom", {"start": v(-50.5, 80) * mm, "end": v(29.5, 80) * mm, "construction": true});
            skLineSegment(sketch, "E108.top", {"start": v(-50.5, 30) * mm, "end": v(29.5, 30) * mm, "construction": true});
            skLineSegment(sketch, "E108.left", {"start": v(-50.5, 80) * mm, "end": v(-50.5, 30) * mm, "construction": true});
            skLineSegment(sketch, "E108.right", {"start": v(29.5, 80) * mm, "end": v(29.5, 30) * mm, "construction": true});
            skLineSegment(sketch, "E109", {"start": v(-81.5, 55) * mm, "end": v(50.5, 55) * mm, "construction": true});
            skCircle(sketch, "E110", {"center": v(-50.5, 80) * mm, "radius": 5.5 * mm});
            skCircle(sketch, "E111", {"center": v(29.5, 80) * mm, "radius": 5.5 * mm});
            skCircle(sketch, "E112", {"center": v(-50.5, 30) * mm, "radius": 5.5 * mm});
            skCircle(sketch, "E113", {"center": v(29.5, 30) * mm, "radius": 5.5 * mm});
            skSolve(sketch);
        }
        {
            var Q0;
            Q0 = qSketchRegion(id + "F33", true);
            extrude(context, id + "F34", {"entities" : qUnion([Q0]), "operationType" : NewBodyOperationType.REMOVE, "endBound" : BoundingType.UP_TO_NEXT, "oppositeDirection" : true, "depth" : 25 * mm});
        }
        {
            var Q0;
            Q0=makeQuery(id+"F31.opExtrude","SWEPT_FACE",FACE,{"disambiguationData":[OSD([sQuery(id+"F30.wireOp",EDGE,"E100")])]});
            var sketch = newSketch(context, id + "F35", { "sketchPlane" : qUnion([Q0])});
            skLineSegment(sketch, "E114", {"start": v(81.5, 55) * mm, "end": v(42.5, 55) * mm, "construction": true});
            skCircle(sketch, "E115", {"center": v(59.5, 80) * mm, "radius": 5.5 * mm});
            skCircle(sketch, "E116", {"center": v(59.5, 30) * mm, "radius": 5.5 * mm});
            skSolve(sketch);
        }
        {
            var Q0;
            Q0 = qSketchRegion(id + "F35", true);
            extrude(context, id + "F36", {"entities" : qUnion([Q0]), "operationType" : NewBodyOperationType.REMOVE, "endBound" : BoundingType.UP_TO_NEXT, "oppositeDirection" : true, "depth" : 25 * mm, "hasSecondDirection" : true, "secondDirectionBound" : SecondDirectionBoundingType.THROUGH_ALL, "secondDirectionOppositeDirection" : false, "secondDirectionDepth" : 25 * mm});
        }
        {
            var Q0;
            Q0=makeQuery(id+"F31.opExtrude","SWEPT_FACE",FACE,{"disambiguationData":[OSD([sQuery(id+"F30.wireOp",EDGE,"E101")])]});
            var sketch = newSketch(context, id + "F37", { "sketchPlane" : qUnion([Q0])});
            skLineSegment(sketch, "E117", {"start": v(311, 100) * mm, "end": v(311, 10) * mm, "construction": true});
            skLineSegment(sketch, "E118", {"start": v(333, 55) * mm, "end": v(289, 55) * mm, "construction": true});
            skCircle(sketch, "E119", {"center": v(311, 90) * mm, "radius": 4.4 * mm});
            skCircle(sketch, "E120", {"center": v(311, 20) * mm, "radius": 4.4 * mm});
            skSolve(sketch);
        }
        {
            var Q0;
            Q0 = qSketchRegion(id + "F37", true);
            extrude(context, id + "F38", {"entities" : qUnion([Q0]), "operationType" : NewBodyOperationType.REMOVE, "endBound" : BoundingType.UP_TO_NEXT, "oppositeDirection" : true, "depth" : 25 * mm});
        }
        {
            var Q0;
            Q0=makeQuery(id+"F22.opPattern","COPY",FACE,{"derivedFrom":makeQuery(id+"F21.opExtrude","CAP_FACE",FACE,{"disambiguationData":[OSD([sQuery(id+"F20.wireOp",EDGE,"E52"),sQuery(id+"F20.wireOp",EDGE,"E53"),sQuery(id+"F20.wireOp",EDGE,"E54"),sQuery(id+"F20.wireOp",EDGE,"E55"),sQuery(id+"F20.wireOp",EDGE,"E56"),sQuery(id+"F20.wireOp",EDGE,"E57"),sQuery(id+"F20.wireOp",EDGE,"E58"),sQuery(id+"F20.wireOp",EDGE,"E59"),sQuery(id+"F20.wireOp",EDGE,"E60"),sQuery(id+"F20.wireOp",EDGE,"E61"),sQuery(id+"F20.wireOp",EDGE,"E62"),sQuery(id+"F20.wireOp",EDGE,"E63"),sQuery(id+"F20.wireOp",EDGE,"E64"),sQuery(id+"F20.wireOp",EDGE,"E65"),sQuery(id+"F20.wireOp",EDGE,"E66"),sQuery(id+"F20.wireOp",EDGE,"E67"),sQuery(id+"F20.wireOp",EDGE,"E68"),sQuery(id+"F20.wireOp",EDGE,"E69"),sQuery(id+"F20.wireOp",EDGE,"E70.filletArc"),sQuery(id+"F20.wireOp",EDGE,"E71.filletArc"),sQuery(id+"F20.wireOp",EDGE,"E72"),sQuery(id+"F20.wireOp",EDGE,"E73"),sQuery(id+"F20.wireOp",EDGE,"E75"),sQuery(id+"F20.wireOp",EDGE,"E77"),sQuery(id+"F20.wireOp",EDGE,"E78")])],"isStart":true}),"instanceName":"1"});
            var sketch = newSketch(context, id + "F39", { "sketchPlane" : qUnion([Q0])});
            skCircle(sketch, "E121", {"center": v(-89.5, -20) * mm, "radius": 10 * mm});
            skCircle(sketch, "E122", {"center": v(-89.5, -20) * mm, "radius": 5 * mm});
            skSolve(sketch);
        }
        {
            var Q0;
            Q0 = qSketchRegion(id + "F39", true);
            extrude(context, id + "F40", {"entities" : qUnion([Q0]), "depth" : 13 * mm});
        }
        {
            var Q0;
            Q0=makeQuery(id+"F40.opExtrude","SWEPT_BODY",BODY,{"disambiguationData":[OSD([sQuery(id+"F39.wireOp",EDGE,"E121"),sQuery(id+"F39.wireOp",EDGE,"E122")])]});
            transform(context, id + "F41", {"entities" : qUnion([Q0]), "transformType" : TransformType.TRANSLATION_3D, "dx" : 625 * mm, "dy" : 0 * mm, "dz" : 0 * mm, "makeCopy" : true});
        }
        {
            var Q0;
            Q0=qCreatedBy(makeId("Front.planeOp"),FACE);
            var sketch = newSketch(context, id + "F42", { "sketchPlane" : qUnion([Q0])});
            skLineSegment(sketch, "E123", {"start": v(-56.83, 135.42) * mm, "end": v(-20.46, 135.42) * mm, "construction": true});
            skLineSegment(sketch, "E124", {"start": v(-52.91, 135.42) * mm, "end": v(-52.91, 140.98) * mm});
            skLineSegment(sketch, "E125", {"start": v(-52.91, 140.98) * mm, "end": v(-27.91, 140.98) * mm});
            skLineSegment(sketch, "E126", {"start": v(-27.91, 140.98) * mm, "end": v(-27.91, 145.67) * mm});
            skLineSegment(sketch, "E127", {"start": v(-27.91, 145.67) * mm, "end": v(-25.41, 145.67) * mm});
            skLineSegment(sketch, "E128", {"start": v(-25.41, 145.67) * mm, "end": v(-25.41, 135.42) * mm});
            skLineSegment(sketch, "E129", {"start": v(-25.41, 135.42) * mm, "end": v(-52.91, 135.42) * mm});
            skSolve(sketch);
        }
        {
            var Q0;
            Q0 = qSketchRegion(id + "F42", true);
            var Q1;
            Q1=sQuery(id+"F42.wireOp",EDGE,"E123");
            revolve(context, id + "F43", {"entities" : qUnion([Q0]), "axis" : qUnion([Q1]), "revolveType" : RevolveType.FULL});
        }
        {
            var Q0;
            Q0=makeQuery(id+"F43.opRevolve","SWEPT_FACE",FACE,{"disambiguationData":[OSD([sQuery(id+"F42.wireOp",EDGE,"E128")])]});
            var sketch = newSketch(context, id + "F44", { "sketchPlane" : qUnion([Q0])});
            skCircle(sketch, "E130.cCircle", {"center": v(0, 135.42) * mm, "radius": 7.5 * mm, "construction": true});
            skLineSegment(sketch, "E130.0", {"start": v(8.66, 135.16) * mm, "end": v(4.1, 127.8) * mm});
            skLineSegment(sketch, "E130.1", {"start": v(4.1, 127.8) * mm, "end": v(-4.55, 128.06) * mm});
            skLineSegment(sketch, "E130.2", {"start": v(-4.55, 128.06) * mm, "end": v(-8.66, 135.68) * mm});
            skLineSegment(sketch, "E130.3", {"start": v(-8.66, 135.68) * mm, "end": v(-4.1, 143.05) * mm});
            skLineSegment(sketch, "E130.4", {"start": v(-4.1, 143.05) * mm, "end": v(4.55, 142.8) * mm});
            skLineSegment(sketch, "E130.5", {"start": v(4.55, 142.8) * mm, "end": v(8.66, 135.16) * mm});
            skPoint(sketch, "E130.0.midPoint", {"position": v(6.38, 131.48) * mm});
            skSolve(sketch);
        }
        {
            var Q0;
            Q0 = qSketchRegion(id + "F44", true);
            var Q1;
            Q1=makeQuery(id+"F44.imprint","IMPRINT",FACE,{"disambiguationData":[TD([[makeQuery(id+"F44.imprint","IMPRINT",EDGE,{"derivedFrom":sQuery(id+"F44.wireOp",EDGE,"E130.0")}),-1.0]])]});
            extrude(context, id + "F45", {"entities" : qUnion([Q0, Q1]), "operationType" : NewBodyOperationType.ADD, "depth" : 6.5 * mm});
        }
        {
            var Q0;
            Q0=makeQuery(id+"F43.opRevolve","SWEPT_EDGE",EDGE,{"disambiguationData":[OSD([sQuery(id+"F42.wireOp",EDGE,"E124"),sQuery(id+"F42.wireOp",EDGE,"E125")])]});
            var Q1;
            Q1=makeQuery(id+"F43.opRevolve","SWEPT_EDGE",EDGE,{"disambiguationData":[OSD([sQuery(id+"F42.wireOp",EDGE,"E127"),sQuery(id+"F42.wireOp",EDGE,"E128")])]});
            chamfer(context, id + "F46", {"entities" : qUnion([Q0, Q1]), "width" : 1 * mm, "tangentPropagation" : true});
        }
        {
            var Q0;
            Q0=makeQuery(id+"F31.opExtrude","CAP_FACE",FACE,{"disambiguationData":[OSD([sQuery(id+"F30.wireOp",EDGE,"E100"),sQuery(id+"F30.wireOp",EDGE,"E101"),sQuery(id+"F30.wireOp",EDGE,"E102"),sQuery(id+"F30.wireOp",EDGE,"E103.filletArc"),sQuery(id+"F30.wireOp",EDGE,"E104.filletArc"),sQuery(id+"F30.wireOp",EDGE,"E105.0"),sQuery(id+"F30.wireOp",EDGE,"E105.1"),sQuery(id+"F30.wireOp",EDGE,"E105.2"),sQuery(id+"F30.wireOp",EDGE,"E105.3"),sQuery(id+"F30.wireOp",EDGE,"E105.4"),sQuery(id+"F30.wireOp",EDGE,"E106"),sQuery(id+"F30.wireOp",EDGE,"E107")])],"isStart":false});
            var sketch = newSketch(context, id + "F47", { "sketchPlane" : qUnion([Q0])});
            skLineSegment(sketch, "E131.0", {"start": v(281, -74.5) * mm, "end": v(275, -74.5) * mm, "construction": true});
            skLineSegment(sketch, "E132", {"start": v(339, -3.29) * mm, "end": v(339, -39.91) * mm});
            skLineSegment(sketch, "E133", {"start": v(339, -39.91) * mm, "end": v(283, -79.12) * mm});
            skLineSegment(sketch, "E134", {"start": v(283, -79.12) * mm, "end": v(283, -42.5) * mm});
            skLineSegment(sketch, "E135", {"start": v(283, -42.5) * mm, "end": v(339, -3.29) * mm});
            skLineSegment(sketch, "E136", {"start": v(311, -89.5) * mm, "end": v(311, 37.52) * mm, "construction": true});
            skSolve(sketch);
        }
        {
            var Q0;
            Q0=makeQuery(id+"F31.opExtrude","CAP_FACE",FACE,{"disambiguationData":[OSD([sQuery(id+"F30.wireOp",EDGE,"E100"),sQuery(id+"F30.wireOp",EDGE,"E101"),sQuery(id+"F30.wireOp",EDGE,"E102"),sQuery(id+"F30.wireOp",EDGE,"E103.filletArc"),sQuery(id+"F30.wireOp",EDGE,"E104.filletArc"),sQuery(id+"F30.wireOp",EDGE,"E105.0"),sQuery(id+"F30.wireOp",EDGE,"E105.1"),sQuery(id+"F30.wireOp",EDGE,"E105.2"),sQuery(id+"F30.wireOp",EDGE,"E105.3"),sQuery(id+"F30.wireOp",EDGE,"E105.4"),sQuery(id+"F30.wireOp",EDGE,"E106"),sQuery(id+"F30.wireOp",EDGE,"E107")])],"isStart":false});
            var Q1;
            Q1=makeQuery(id+"F31.opExtrude","CAP_FACE",FACE,{"disambiguationData":[OSD([sQuery(id+"F30.wireOp",EDGE,"E100"),sQuery(id+"F30.wireOp",EDGE,"E101"),sQuery(id+"F30.wireOp",EDGE,"E102"),sQuery(id+"F30.wireOp",EDGE,"E103.filletArc"),sQuery(id+"F30.wireOp",EDGE,"E104.filletArc"),sQuery(id+"F30.wireOp",EDGE,"E105.0"),sQuery(id+"F30.wireOp",EDGE,"E105.1"),sQuery(id+"F30.wireOp",EDGE,"E105.2"),sQuery(id+"F30.wireOp",EDGE,"E105.3"),sQuery(id+"F30.wireOp",EDGE,"E105.4"),sQuery(id+"F30.wireOp",EDGE,"E106"),sQuery(id+"F30.wireOp",EDGE,"E107")])],"isStart":true});
            cPlane(context, id + "F48", {"entities" : qUnion([Q0, Q1]), "cplaneType" : CPlaneType.MID_PLANE, "offset" : 150 * mm, "width" : 150 * mm, "height" : 150 * mm});
        }
        {
            var Q0;
            Q0=makeQuery(id+"F1.opExtrude","SWEPT_EDGE",EDGE,{"disambiguationData":[OSD([sQuery(id+"F0.wireOp",EDGE,"E2"),sQuery(id+"F0.wireOp",EDGE,"E5")])]});
            cPlane(context, id + "F49", {"entities" : qUnion([Q0]), "cplaneType" : CPlaneType.MID_PLANE, "offset" : 150 * mm, "width" : 150 * mm, "height" : 150 * mm});
        }
        {
            var Q0;
            Q0=makeQuery(id+"F31.opExtrude","SWEPT_BODY",BODY,{"disambiguationData":[OSD([sQuery(id+"F30.wireOp",EDGE,"E100"),sQuery(id+"F30.wireOp",EDGE,"E101"),sQuery(id+"F30.wireOp",EDGE,"E102"),sQuery(id+"F30.wireOp",EDGE,"E103.filletArc"),sQuery(id+"F30.wireOp",EDGE,"E104.filletArc"),sQuery(id+"F30.wireOp",EDGE,"E105.0"),sQuery(id+"F30.wireOp",EDGE,"E105.1"),sQuery(id+"F30.wireOp",EDGE,"E105.2"),sQuery(id+"F30.wireOp",EDGE,"E105.3"),sQuery(id+"F30.wireOp",EDGE,"E105.4"),sQuery(id+"F30.wireOp",EDGE,"E106"),sQuery(id+"F30.wireOp",EDGE,"E107")])]});
            var Q1;
            Q1=qCreatedBy(id+"F49.planeOp",FACE);
            mirror(context, id + "F50", {"entities" : qUnion([Q0]), "mirrorPlane" : qUnion([Q1])});
        }
        {
            var Q0;
            Q0=makeQuery(id+"F1.opExtrude","SWEPT_FACE",FACE,{"disambiguationData":[OSD([sQuery(id+"F0.wireOp",EDGE,"E1")])]});
            var sketch = newSketch(context, id + "F51", { "sketchPlane" : qUnion([Q0])});
            skCircle(sketch, "E137.cCircle", {"center": v(-127, 31.5) * mm, "radius": 8.5 * mm, "construction": true});
            skLineSegment(sketch, "E137.0", {"start": v(-135.5, 26.6) * mm, "end": v(-135.5, 36.4) * mm});
            skLineSegment(sketch, "E137.1", {"start": v(-135.5, 36.4) * mm, "end": v(-127, 41.31) * mm});
            skLineSegment(sketch, "E137.2", {"start": v(-127, 41.31) * mm, "end": v(-118.5, 36.4) * mm});
            skLineSegment(sketch, "E137.3", {"start": v(-118.5, 36.4) * mm, "end": v(-118.5, 26.6) * mm});
            skLineSegment(sketch, "E137.4", {"start": v(-118.5, 26.6) * mm, "end": v(-127, 21.69) * mm});
            skLineSegment(sketch, "E137.5", {"start": v(-127, 21.69) * mm, "end": v(-135.5, 26.6) * mm});
            skPoint(sketch, "E137.0.midPoint", {"position": v(-135.5, 31.5) * mm});
            skCircle(sketch, "E138", {"center": v(-127, 31.5) * mm, "radius": 4.25 * mm});
            skSolve(sketch);
        }
        {
            var Q0;
            Q0 = qSketchRegion(id + "F51", true);
            extrude(context, id + "F52", {"entities" : qUnion([Q0]), "depth" : 7 * mm});
        }
        {
            var Q0;
            Q0=makeQuery(id+"F1.opExtrude","SWEPT_FACE",FACE,{"disambiguationData":[OSD([sQuery(id+"F0.wireOp",EDGE,"E1")])]});
            var sketch = newSketch(context, id + "F53", { "sketchPlane" : qUnion([Q0])});
            skCircle(sketch, "E139", {"center": v(-140, 50.1) * mm, "radius": 5.4 * mm});
            skCircle(sketch, "E140.cCircle", {"center": v(-140, 50.1) * mm, "radius": 9.5 * mm, "construction": true});
            skLineSegment(sketch, "E140.0", {"start": v(-149.5, 44.62) * mm, "end": v(-149.5, 55.58) * mm});
            skLineSegment(sketch, "E140.1", {"start": v(-149.5, 55.58) * mm, "end": v(-140, 61.07) * mm});
            skLineSegment(sketch, "E140.2", {"start": v(-140, 61.07) * mm, "end": v(-130.5, 55.58) * mm});
            skLineSegment(sketch, "E140.3", {"start": v(-130.5, 55.58) * mm, "end": v(-130.5, 44.62) * mm});
            skLineSegment(sketch, "E140.4", {"start": v(-130.5, 44.62) * mm, "end": v(-140, 39.13) * mm});
            skLineSegment(sketch, "E140.5", {"start": v(-140, 39.13) * mm, "end": v(-149.5, 44.62) * mm});
            skPoint(sketch, "E140.0.midPoint", {"position": v(-149.5, 50.1) * mm});
            skSolve(sketch);
        }
        {
            var Q0;
            Q0 = qSketchRegion(id + "F53", true);
            extrude(context, id + "F54", {"entities" : qUnion([Q0]), "depth" : 7 * mm});
        }
        {
            var Q0;
            Q0=makeQuery(id+"F1.opExtrude","SWEPT_FACE",FACE,{"disambiguationData":[OSD([sQuery(id+"F0.wireOp",EDGE,"E3.0")])]});
            var sketch = newSketch(context, id + "F55", { "sketchPlane" : qUnion([Q0])});
            skLineSegment(sketch, "E141", {"start": v(-127.5, 44.85) * mm, "end": v(127.5, 44.85) * mm, "construction": true});
            skLineSegment(sketch, "E142", {"start": v(-107, 75.85) * mm, "end": v(-148.5, 61.25) * mm});
            skCircle(sketch, "E143", {"center": v(-127.5, 44.85) * mm, "radius": 6.65 * mm});
            skLineSegment(sketch, "E144.MirrorCS", {"start": v(107, 75.85) * mm, "end": v(148.5, 61.25) * mm});
            skCircle(sketch, "E145.MirrorC", {"center": v(127.5, 44.85) * mm, "radius": 6.65 * mm});
            skLineSegment(sketch, "E146.MirrorCS", {"start": v(-107, 13.85) * mm, "end": v(-148.5, 28.45) * mm});
            skLineSegment(sketch, "E147.MirrorCS", {"start": v(107, 13.85) * mm, "end": v(148.5, 28.45) * mm});
            skLineSegment(sketch, "E148", {"start": v(-107, 75.85) * mm, "end": v(107, 75.85) * mm});
            skLineSegment(sketch, "E149", {"start": v(-107, 13.85) * mm, "end": v(107, 13.85) * mm});
            skCircle(sketch, "E150", {"center": v(-87.9, 44.85) * mm, "radius": 12.1 * mm});
            skCircle(sketch, "E151.MirrorC", {"center": v(87.9, 44.85) * mm, "radius": 12.1 * mm});
            skLineSegment(sketch, "E152", {"start": v(-87.9, 56.95) * mm, "end": v(87.9, 56.95) * mm});
            skLineSegment(sketch, "E153.MirrorCS", {"start": v(-87.9, 32.75) * mm, "end": v(87.9, 32.75) * mm});
            skLineSegment(sketch, "E154", {"start": v(-148.5, 61.25) * mm, "end": v(-148.5, 28.45) * mm});
            skLineSegment(sketch, "E155", {"start": v(148.5, 61.25) * mm, "end": v(148.5, 28.45) * mm});
            skSolve(sketch);
        }
        {
            var Q0;
            Q0 = qSketchRegion(id + "F55", true);
            extrude(context, id + "F56", {"entities" : qUnion([Q0]), "depth" : 18 * mm});
        }
        {
            var Q0;
            Q0=makeQuery(id+"F56.opExtrude","CAP_FACE",FACE,{"disambiguationData":[OSD([sQuery(id+"F55.wireOp",EDGE,"1EFQZ6ap-uAg3-N8OW-0aFA-wIDavsOpqr7z"),sQuery(id+"F55.wireOp",EDGE,"E142"),sQuery(id+"F55.wireOp",EDGE,"E143"),sQuery(id+"F55.wireOp",EDGE,"E144.MirrorCS"),sQuery(id+"F55.wireOp",EDGE,"E145.MirrorC"),sQuery(id+"F55.wireOp",EDGE,"dfcf7d93-0b25-4aa2-80d3-010f8d92ff410.MirrorC"),sQuery(id+"F55.wireOp",EDGE,"E146.MirrorCS"),sQuery(id+"F55.wireOp",EDGE,"E147.MirrorCS"),sQuery(id+"F55.wireOp",EDGE,"E148"),sQuery(id+"F55.wireOp",EDGE,"E149"),sQuery(id+"F55.wireOp",EDGE,"E150"),sQuery(id+"F55.wireOp",EDGE,"E151.MirrorC"),sQuery(id+"F55.wireOp",EDGE,"E152"),sQuery(id+"F55.wireOp",EDGE,"E153.MirrorCS")])],"isStart":false});
            var sketch = newSketch(context, id + "F57", { "sketchPlane" : qUnion([Q0])});
            skCircle(sketch, "E156", {"center": v(-127.5, 44.85) * mm, "radius": 12.6 * mm});
            skCircle(sketch, "E157", {"center": v(127.5, 44.85) * mm, "radius": 12.6 * mm});
            skSolve(sketch);
        }
        {
            var Q0;
            Q0 = qSketchRegion(id + "F57", true);
            extrude(context, id + "F58", {"entities" : qUnion([Q0]), "operationType" : NewBodyOperationType.REMOVE, "oppositeDirection" : true, "depth" : 11.5 * mm});
        }
        {
            var Q0;
            Q0=makeQuery(id+"F56.opExtrude","CAP_EDGE",EDGE,{"disambiguationData":[OSD([sQuery(id+"F55.wireOp",EDGE,"E151.MirrorC")])],"isStart":false});
            var Q1;
            Q1=makeQuery(id+"F56.opExtrude","CAP_EDGE",EDGE,{"disambiguationData":[OSD([sQuery(id+"F55.wireOp",EDGE,"E153.MirrorCS")])],"isStart":true});
            fillet(context, id + "F59", {"entities" : qUnion([Q0, Q1]), "radius" : 7 * mm, "tangentPropagation" : true, "allowEdgeOverflow" : false});
        }
        {
            var Q0;
            Q0=makeQuery(id+"F56.opExtrude","SWEPT_EDGE",EDGE,{"disambiguationData":[OSD([sQuery(id+"F55.wireOp",EDGE,"E142"),sQuery(id+"F55.wireOp",EDGE,"E148")])]});
            var Q1;
            Q1=makeQuery(id+"F56.opExtrude","SWEPT_EDGE",EDGE,{"disambiguationData":[OSD([sQuery(id+"F55.wireOp",EDGE,"E144.MirrorCS"),sQuery(id+"F55.wireOp",EDGE,"E148")])]});
            var Q2;
            Q2=makeQuery(id+"F56.opExtrude","SWEPT_EDGE",EDGE,{"disambiguationData":[OSD([sQuery(id+"F55.wireOp",EDGE,"E146.MirrorCS"),sQuery(id+"F55.wireOp",EDGE,"E149")])]});
            var Q3;
            Q3=makeQuery(id+"F56.opExtrude","SWEPT_EDGE",EDGE,{"disambiguationData":[OSD([sQuery(id+"F55.wireOp",EDGE,"E147.MirrorCS"),sQuery(id+"F55.wireOp",EDGE,"E149")])]});
            var Q4;
            Q4=makeQuery(id+"F56.opExtrude","SWEPT_EDGE",EDGE,{"disambiguationData":[OSD([sQuery(id+"F55.wireOp",EDGE,"E142"),sQuery(id+"F55.wireOp",EDGE,"E154")])]});
            var Q5;
            Q5=makeQuery(id+"F56.opExtrude","SWEPT_EDGE",EDGE,{"disambiguationData":[OSD([sQuery(id+"F55.wireOp",EDGE,"E146.MirrorCS"),sQuery(id+"F55.wireOp",EDGE,"E154")])]});
            var Q6;
            Q6=makeQuery(id+"F56.opExtrude","SWEPT_EDGE",EDGE,{"disambiguationData":[OSD([sQuery(id+"F55.wireOp",EDGE,"E144.MirrorCS"),sQuery(id+"F55.wireOp",EDGE,"E155")])]});
            var Q7;
            Q7=makeQuery(id+"F56.opExtrude","SWEPT_EDGE",EDGE,{"disambiguationData":[OSD([sQuery(id+"F55.wireOp",EDGE,"E147.MirrorCS"),sQuery(id+"F55.wireOp",EDGE,"E155")])]});
            fillet(context, id + "F60", {"entities" : qUnion([Q0, Q1, Q2, Q3, Q4, Q5, Q6, Q7]), "radius" : 18 * mm, "tangentPropagation" : true, "allowEdgeOverflow" : false});
        }
        {
            var Q0;
            Q0=makeQuery(id+"F29.opExtrude","SWEPT_FACE",FACE,{"disambiguationData":[OSD([sQuery(id+"F28.wireOp",EDGE,"E99.right")])]});
            var sketch = newSketch(context, id + "F61", { "sketchPlane" : qUnion([Q0])});
            skLineSegment(sketch, "E158.bottom", {"start": v(354, -30) * mm, "end": v(364, -30) * mm});
            skLineSegment(sketch, "E158.top", {"start": v(354, -70) * mm, "end": v(364, -70) * mm});
            skLineSegment(sketch, "E158.left", {"start": v(354, -30) * mm, "end": v(354, -70) * mm});
            skLineSegment(sketch, "E158.right", {"start": v(364, -30) * mm, "end": v(364, -70) * mm});
            skSolve(sketch);
        }
        {
            var Q0;
            {var subQ4=sQuery(id+"F61.wireOp",EDGE,"E158.bottom");Q0=makeQuery(id+"F61.imprint","IMPRINT",FACE,{"disambiguationData":[TD([[makeQuery(id+"F61.imprint","IMPRINT",EDGE,{"derivedFrom":subQ4}),-1.0]])]});}
            extrude(context, id + "F62", {"entities" : qUnion([Q0]), "oppositeDirection" : true, "depth" : 10 * mm});
        }
        {
            var Q0;
            Q0=makeQuery(id+"F62.opExtrude","SWEPT_EDGE",EDGE,{"disambiguationData":[OSD([sQuery(id+"F61.wireOp",EDGE,"E158.top"),sQuery(id+"F61.wireOp",EDGE,"E158.right")])]});
            var Q1;
            Q1=makeQuery(id+"F62.opExtrude","CAP_EDGE",EDGE,{"disambiguationData":[OSD([sQuery(id+"F61.wireOp",EDGE,"E158.top")])],"isStart":true});
            var Q2;
            Q2=makeQuery(id+"F62.opExtrude","SWEPT_EDGE",EDGE,{"disambiguationData":[OSD([sQuery(id+"F61.wireOp",EDGE,"E158.top"),sQuery(id+"F61.wireOp",EDGE,"E158.left")])]});
            var Q3;
            Q3=makeQuery(id+"F62.opExtrude","CAP_EDGE",EDGE,{"disambiguationData":[OSD([sQuery(id+"F61.wireOp",EDGE,"E158.top")])],"isStart":false});
            chamfer(context, id + "F63", {"entities" : qUnion([Q0, Q1, Q2, Q3]), "width" : 2 * mm, "tangentPropagation" : true});
        }
        {
            var Q0;
            Q0=makeQuery(id+"F62.opExtrude","SWEPT_BODY",BODY,{"disambiguationData":[OSD([sQuery(id+"F61.wireOp",EDGE,"E158.bottom"),sQuery(id+"F61.wireOp",EDGE,"E158.top"),sQuery(id+"F61.wireOp",EDGE,"E158.left"),sQuery(id+"F61.wireOp",EDGE,"E158.right")])]});
            var Q1;
            Q1=qCreatedBy(id+"F49.planeOp",FACE);
            mirror(context, id + "F64", {"entities" : qUnion([Q0]), "mirrorPlane" : qUnion([Q1])});
        }
    });
